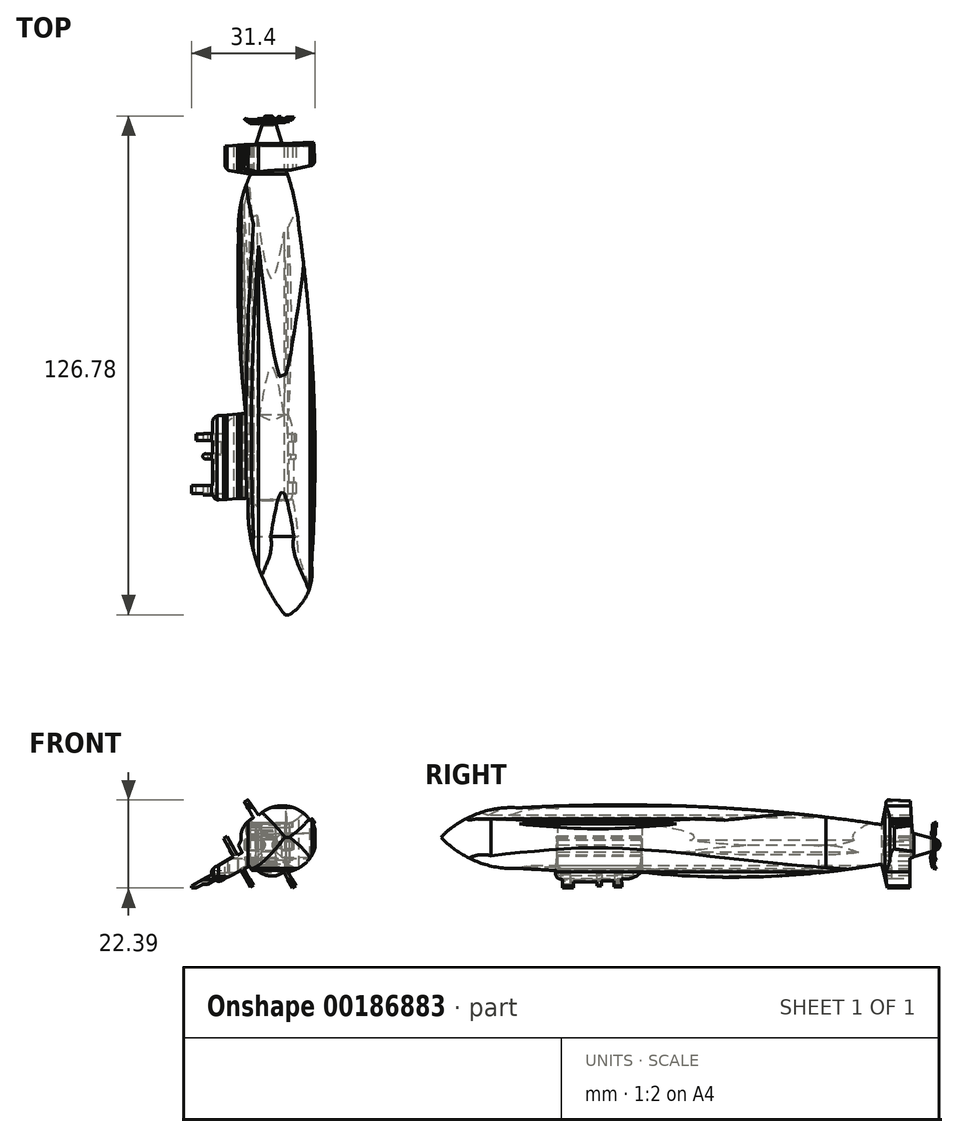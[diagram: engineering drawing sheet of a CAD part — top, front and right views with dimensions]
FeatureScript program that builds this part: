
annotation { "Feature Type Name" : "Feature", "Feature Type Description" : "" }
export const myFeature = defineFeature(function(context is Context, id is Id, definition is map)
    precondition{}
    {
        {
            var Q0;
            Q0=qCreatedBy(makeId("Front.planeOp"),FACE);
            var sketch = newSketch(context, id + "F0", { "sketchPlane" : qUnion([Q0])});
            skLineSegment(sketch, "E0.bottom", {"start": v(0, 0) * mm, "end": v(32, 0) * mm});
            skLineSegment(sketch, "E0.top", {"start": v(0, 23) * mm, "end": v(32, 23) * mm});
            skLineSegment(sketch, "E0.left", {"start": v(0, 0) * mm, "end": v(0, 23) * mm});
            skLineSegment(sketch, "E0.right", {"start": v(32, 0) * mm, "end": v(32, 23) * mm});
            skSolve(sketch);
        }
        {
            var Q0;
            Q0=makeQuery(id+"F0.imprint","IMPRINT",FACE,{"disambiguationData":[TD([[makeQuery(id+"F0.imprint","IMPRINT",EDGE,{"derivedFrom":sQuery(id+"F0.wireOp",EDGE,"E0.bottom")}),1.0]])]});
            extrude(context, id + "F1", {"entities" : qUnion([Q0]), "depth" : 128 * mm});
        }
        {
            var Q0;
            Q0=makeQuery(id+"F1.opExtrude","CAP_FACE",FACE,{"disambiguationData":[OSD([sQuery(id+"F0.wireOp",EDGE,"E0.bottom"),sQuery(id+"F0.wireOp",EDGE,"E0.top"),sQuery(id+"F0.wireOp",EDGE,"E0.left"),sQuery(id+"F0.wireOp",EDGE,"E0.right")])],"isStart":false});
            var sketch = newSketch(context, id + "F2", { "sketchPlane" : qUnion([Q0])});
            skArc(sketch, "E1", {"start": v(30.16, 17.5) * mm, "mid": v(23.9, 21.12) * mm, "end": v(17.06, 18.74) * mm});
            skArc(sketch, "E2", {"start": v(24.47, 4.4) * mm, "mid": v(30.73, 8.86) * mm, "end": v(30.92, 16.54) * mm});
            skArc(sketch, "E3", {"start": v(15.8, 18.1) * mm, "mid": v(13.22, 15.75) * mm, "end": v(12.66, 12.3) * mm});
            skArc(sketch, "E4", {"start": v(16.72, 4.8) * mm, "mid": v(20, 3.32) * mm, "end": v(23.48, 4.27) * mm});
            skArc(sketch, "E5", {"start": v(6.51, 5.84) * mm, "mid": v(5.36, 5.04) * mm, "end": v(5.1, 3.67) * mm});
            skArc(sketch, "E6", {"start": v(5.95, 2.34) * mm, "mid": v(7.24, 1.97) * mm, "end": v(8.4, 2.62) * mm});
            skLineSegment(sketch, "E7", {"start": v(15.8, 18.1) * mm, "end": v(13.43, 22.11) * mm});
            skLineSegment(sketch, "E8", {"start": v(13.43, 22.11) * mm, "end": v(14.36, 22.66) * mm});
            skLineSegment(sketch, "E9", {"start": v(14.36, 22.66) * mm, "end": v(17.06, 18.74) * mm});
            skLineSegment(sketch, "E10", {"start": v(30.16, 17.5) * mm, "end": v(30.65, 17.88) * mm});
            skLineSegment(sketch, "E11", {"start": v(30.65, 17.88) * mm, "end": v(31.35, 16.97) * mm});
            skLineSegment(sketch, "E12", {"start": v(31.35, 16.97) * mm, "end": v(30.92, 16.54) * mm});
            skLineSegment(sketch, "E13", {"start": v(24.47, 4.4) * mm, "end": v(26.52, 0.83) * mm});
            skLineSegment(sketch, "E14", {"start": v(26.52, 0.83) * mm, "end": v(25.64, 0.32) * mm});
            skLineSegment(sketch, "E15", {"start": v(25.64, 0.32) * mm, "end": v(23.48, 4.27) * mm});
            skLineSegment(sketch, "E16", {"start": v(12.66, 12.3) * mm, "end": v(11.92, 11.1) * mm});
            skLineSegment(sketch, "E17", {"start": v(11.92, 11.1) * mm, "end": v(12.92, 9.27) * mm});
            skLineSegment(sketch, "E18", {"start": v(12.92, 9.27) * mm, "end": v(11.77, 8.61) * mm});
            skLineSegment(sketch, "E19", {"start": v(11.77, 8.61) * mm, "end": v(9.03, 13.36) * mm});
            skLineSegment(sketch, "E20", {"start": v(9.03, 13.36) * mm, "end": v(8.12, 12.84) * mm});
            skLineSegment(sketch, "E21", {"start": v(8.12, 12.84) * mm, "end": v(10.64, 8.24) * mm});
            skLineSegment(sketch, "E22", {"start": v(10.64, 8.24) * mm, "end": v(6.51, 5.84) * mm});
            skLineSegment(sketch, "E23", {"start": v(5.1, 3.67) * mm, "end": v(0, 0.87) * mm});
            skLineSegment(sketch, "E24", {"start": v(0, 0.87) * mm, "end": v(0.73, 0) * mm});
            skLineSegment(sketch, "E25", {"start": v(0.73, 0) * mm, "end": v(2.91, 1.2) * mm});
            skLineSegment(sketch, "E26", {"start": v(2.91, 1.2) * mm, "end": v(4.06, 1.2) * mm});
            skLineSegment(sketch, "E27", {"start": v(4.06, 1.2) * mm, "end": v(5.95, 2.34) * mm});
            skLineSegment(sketch, "E28", {"start": v(8.4, 2.62) * mm, "end": v(12.66, 4.73) * mm});
            skLineSegment(sketch, "E29", {"start": v(12.66, 4.73) * mm, "end": v(15.01, 0.43) * mm});
            skLineSegment(sketch, "E30", {"start": v(15.01, 0.43) * mm, "end": v(15.8, 0.89) * mm});
            skLineSegment(sketch, "E31", {"start": v(15.8, 0.89) * mm, "end": v(13.39, 5.08) * mm});
            skLineSegment(sketch, "E32", {"start": v(13.39, 5.08) * mm, "end": v(14.7, 5.84) * mm});
            skLineSegment(sketch, "E33", {"start": v(14.7, 5.84) * mm, "end": v(15.34, 4.73) * mm});
            skLineSegment(sketch, "E34", {"start": v(15.34, 4.73) * mm, "end": v(16.72, 4.8) * mm});
            skLineSegment(sketch, "E35.bottom", {"start": v(32, 0) * mm, "end": v(0, 0) * mm});
            skLineSegment(sketch, "E35.top", {"start": v(32, 23) * mm, "end": v(0, 23) * mm});
            skLineSegment(sketch, "E35.left", {"start": v(32, 0) * mm, "end": v(32, 23) * mm});
            skLineSegment(sketch, "E35.right", {"start": v(0, 0) * mm, "end": v(0, 23) * mm});
            skSolve(sketch);
        }
        {
            var Q0;
            Q0=makeQuery(id+"F1.opExtrude","SWEPT_FACE",FACE,{"disambiguationData":[OSD([sQuery(id+"F0.wireOp",EDGE,"E0.right")])]});
            var sketch = newSketch(context, id + "F3", { "sketchPlane" : qUnion([Q0])});
            skArc(sketch, "E36", {"start": v(-107, 20.64) * mm, "mid": v(-117.76, 19.1) * mm, "end": v(-126.88, 13.18) * mm});
            skArc(sketch, "E37", {"start": v(-126.88, 13.18) * mm, "mid": v(-117.83, 7) * mm, "end": v(-107, 5.25) * mm});
            skArc(sketch, "E38", {"start": v(-14.85, 16.34) * mm, "mid": v(-60.81, 20.9) * mm, "end": v(-107, 20.64) * mm});
            skArc(sketch, "E39", {"start": v(-76.03, 4.3) * mm, "mid": v(-45.41, 3.13) * mm, "end": v(-14.95, 6.4) * mm});
            skArc(sketch, "E40", {"start": v(-97.6, 4.69) * mm, "mid": v(-102.3, 4.98) * mm, "end": v(-107, 5.25) * mm});
            skArc(sketch, "E41", {"start": v(-80.98, 2.6) * mm, "mid": v(-78.3, 2.84) * mm, "end": v(-76.03, 4.3) * mm});
            skArc(sketch, "E42", {"start": v(-97.6, 4.69) * mm, "mid": v(-97.48, 3.09) * mm, "end": v(-95.98, 2.52) * mm});
            skArc(sketch, "E43", {"start": v(-12.67, 22.6) * mm, "mid": v(-13.6, 22.45) * mm, "end": v(-13.82, 21.53) * mm});
            skArc(sketch, "E44", {"start": v(-1.45, 9.87) * mm, "mid": v(-0.1, 11.16) * mm, "end": v(-1.28, 12.6) * mm});
            skLineSegment(sketch, "E45", {"start": v(-95.98, 2.52) * mm, "end": v(-95.98, 0.27) * mm});
            skLineSegment(sketch, "E46", {"start": v(-95.98, 0.27) * mm, "end": v(-93.2, 0.27) * mm});
            skLineSegment(sketch, "E47", {"start": v(-93.2, 0.27) * mm, "end": v(-93.2, 1.83) * mm});
            skLineSegment(sketch, "E48", {"start": v(-93.2, 1.83) * mm, "end": v(-87.22, 1.83) * mm});
            skLineSegment(sketch, "E49", {"start": v(-87.22, 1.83) * mm, "end": v(-87.22, 0.87) * mm});
            skLineSegment(sketch, "E50", {"start": v(-87.22, 0.87) * mm, "end": v(-86.1, 0.87) * mm});
            skLineSegment(sketch, "E51", {"start": v(-86.1, 0.87) * mm, "end": v(-86.1, 2.04) * mm});
            skLineSegment(sketch, "E52", {"start": v(-86.1, 2.04) * mm, "end": v(-82.87, 2.04) * mm});
            skLineSegment(sketch, "E53", {"start": v(-82.87, 2.04) * mm, "end": v(-82.87, 0.54) * mm});
            skLineSegment(sketch, "E54", {"start": v(-82.87, 0.54) * mm, "end": v(-80.96, 0.54) * mm});
            skLineSegment(sketch, "E55", {"start": v(-80.96, 0.54) * mm, "end": v(-80.98, 2.6) * mm});
            skLineSegment(sketch, "E56", {"start": v(-13.82, 21.53) * mm, "end": v(-14.85, 16.34) * mm});
            skLineSegment(sketch, "E57", {"start": v(-12.67, 22.6) * mm, "end": v(-7.65, 22.39) * mm});
            skLineSegment(sketch, "E58", {"start": v(-7.65, 22.39) * mm, "end": v(-7.16, 14.2) * mm});
            skLineSegment(sketch, "E59", {"start": v(-7.16, 14.2) * mm, "end": v(-2.04, 12.84) * mm});
            skLineSegment(sketch, "E60", {"start": v(-2.04, 12.84) * mm, "end": v(-2.04, 13.5) * mm});
            skLineSegment(sketch, "E61", {"start": v(-2.04, 13.5) * mm, "end": v(-2.24, 13.63) * mm});
            skLineSegment(sketch, "E62", {"start": v(-2.24, 13.63) * mm, "end": v(-2.24, 14.68) * mm});
            skLineSegment(sketch, "E63", {"start": v(-2.24, 14.68) * mm, "end": v(-2.05, 14.98) * mm});
            skLineSegment(sketch, "E64", {"start": v(-2.05, 14.98) * mm, "end": v(-2.05, 16.5) * mm});
            skLineSegment(sketch, "E65", {"start": v(-2.05, 16.5) * mm, "end": v(-1.7, 16.77) * mm});
            skLineSegment(sketch, "E66", {"start": v(-1.7, 16.77) * mm, "end": v(-0.96, 16.98) * mm});
            skLineSegment(sketch, "E67", {"start": v(-0.96, 16.98) * mm, "end": v(-0.96, 15.6) * mm});
            skLineSegment(sketch, "E68", {"start": v(-0.96, 15.6) * mm, "end": v(-1.24, 15.6) * mm});
            skLineSegment(sketch, "E69", {"start": v(-1.24, 15.6) * mm, "end": v(-1.24, 13.99) * mm});
            skLineSegment(sketch, "E70", {"start": v(-1.24, 13.99) * mm, "end": v(-1.53, 13.41) * mm});
            skLineSegment(sketch, "E71", {"start": v(-1.53, 13.41) * mm, "end": v(-1.53, 12.84) * mm});
            skLineSegment(sketch, "E72", {"start": v(-1.53, 12.84) * mm, "end": v(-1.28, 12.6) * mm});
            skLineSegment(sketch, "E73", {"start": v(-1.45, 9.87) * mm, "end": v(-1.45, 8.08) * mm});
            skLineSegment(sketch, "E74", {"start": v(-1.45, 8.08) * mm, "end": v(-1.28, 8.04) * mm});
            skLineSegment(sketch, "E75", {"start": v(-1.28, 8.04) * mm, "end": v(-0.97, 7.47) * mm});
            skLineSegment(sketch, "E76", {"start": v(-0.97, 7.47) * mm, "end": v(-1.45, 7.2) * mm});
            skLineSegment(sketch, "E77", {"start": v(-1.45, 7.2) * mm, "end": v(-1.28, 6.87) * mm});
            skLineSegment(sketch, "E78", {"start": v(-1.28, 6.87) * mm, "end": v(-1.53, 6.74) * mm});
            skLineSegment(sketch, "E79", {"start": v(-1.53, 6.74) * mm, "end": v(-1.61, 6.12) * mm});
            skLineSegment(sketch, "E80", {"start": v(-1.61, 6.12) * mm, "end": v(-1.28, 5.79) * mm});
            skLineSegment(sketch, "E81", {"start": v(-1.28, 5.79) * mm, "end": v(-1.07, 5.09) * mm});
            skLineSegment(sketch, "E82", {"start": v(-1.07, 5.09) * mm, "end": v(-1.53, 5.2) * mm});
            skLineSegment(sketch, "E83", {"start": v(-1.53, 5.2) * mm, "end": v(-1.92, 5.31) * mm});
            skLineSegment(sketch, "E84", {"start": v(-1.92, 5.31) * mm, "end": v(-2.12, 5.72) * mm});
            skLineSegment(sketch, "E85", {"start": v(-2.12, 5.72) * mm, "end": v(-2.14, 6.03) * mm});
            skLineSegment(sketch, "E86", {"start": v(-2.14, 6.03) * mm, "end": v(-2.33, 6.22) * mm});
            skLineSegment(sketch, "E87", {"start": v(-2.33, 6.22) * mm, "end": v(-2.45, 7.34) * mm});
            skLineSegment(sketch, "E88", {"start": v(-2.45, 7.34) * mm, "end": v(-2.52, 8.06) * mm});
            skLineSegment(sketch, "E89", {"start": v(-2.52, 8.06) * mm, "end": v(-2.11, 9.6) * mm});
            skLineSegment(sketch, "E90", {"start": v(-2.11, 9.6) * mm, "end": v(-7.7, 7.84) * mm});
            skLineSegment(sketch, "E91", {"start": v(-7.7, 7.84) * mm, "end": v(-7.7, 0.27) * mm});
            skLineSegment(sketch, "E92", {"start": v(-7.7, 0.27) * mm, "end": v(-13.5, 0.27) * mm});
            skLineSegment(sketch, "E93", {"start": v(-13.5, 0.27) * mm, "end": v(-14.95, 6.4) * mm});
            skLineSegment(sketch, "E94.bottom", {"start": v(0, 0) * mm, "end": v(-128, 0) * mm});
            skLineSegment(sketch, "E94.top", {"start": v(0, 23) * mm, "end": v(-128, 23) * mm});
            skLineSegment(sketch, "E94.left", {"start": v(0, 0) * mm, "end": v(0, 23) * mm});
            skLineSegment(sketch, "E94.right", {"start": v(-128, 0) * mm, "end": v(-128, 23) * mm});
            skSolve(sketch);
        }
        {
            var Q0;
            Q0=makeQuery(id+"F1.opExtrude","SWEPT_FACE",FACE,{"disambiguationData":[OSD([sQuery(id+"F0.wireOp",EDGE,"E0.top")])]});
            var sketch = newSketch(context, id + "F4", { "sketchPlane" : qUnion([Q0])});
            skArc(sketch, "E95", {"start": v(14.45, -97.2) * mm, "mid": v(16.46, -113.17) * mm, "end": v(24.1, -127.33) * mm});
            skArc(sketch, "E96", {"start": v(24.1, -127.33) * mm, "mid": v(29.36, -121.77) * mm, "end": v(30.52, -114.21) * mm});
            skArc(sketch, "E97", {"start": v(30.52, -114.21) * mm, "mid": v(31.11, -71.55) * mm, "end": v(27.4, -29.05) * mm});
            skArc(sketch, "E98", {"start": v(27.4, -29.05) * mm, "mid": v(26.22, -21.46) * mm, "end": v(24.1, -14.07) * mm});
            skArc(sketch, "E99", {"start": v(15.08, -14.85) * mm, "mid": v(12.5, -22.7) * mm, "end": v(11.96, -30.92) * mm});
            skArc(sketch, "E100", {"start": v(11.96, -30.92) * mm, "mid": v(12.06, -53.34) * mm, "end": v(13.83, -75.68) * mm});
            skArc(sketch, "E101", {"start": v(5.56, -96.4) * mm, "mid": v(5.9, -97.3) * mm, "end": v(6.83, -97.63) * mm});
            skArc(sketch, "E102", {"start": v(7, -76.26) * mm, "mid": v(5.8, -76.77) * mm, "end": v(5.42, -78) * mm});
            skArc(sketch, "E103", {"start": v(3.64, -85.92) * mm, "mid": v(2.9, -86.48) * mm, "end": v(3.38, -87.27) * mm});
            skArc(sketch, "E104", {"start": v(30.1, -12.79) * mm, "mid": v(30.9, -12.48) * mm, "end": v(31.3, -11.7) * mm});
            skArc(sketch, "E105", {"start": v(8.5, -12.25) * mm, "mid": v(8.78, -13.37) * mm, "end": v(9.71, -14.04) * mm});
            skArc(sketch, "E106", {"start": v(20.92, -0.76) * mm, "mid": v(19.6, 0.16) * mm, "end": v(18.3, -0.79) * mm});
            skLineSegment(sketch, "E107", {"start": v(20.92, -0.76) * mm, "end": v(21.7, -0.76) * mm});
            skLineSegment(sketch, "E108", {"start": v(21.7, -0.76) * mm, "end": v(22.02, -0.33) * mm});
            skLineSegment(sketch, "E109", {"start": v(22.02, -0.33) * mm, "end": v(22.76, -0.33) * mm});
            skLineSegment(sketch, "E110", {"start": v(22.76, -0.33) * mm, "end": v(22.76, -0.76) * mm});
            skLineSegment(sketch, "E111", {"start": v(22.76, -0.76) * mm, "end": v(23.78, -0.76) * mm});
            skLineSegment(sketch, "E112", {"start": v(23.78, -0.76) * mm, "end": v(24.13, -0.45) * mm});
            skLineSegment(sketch, "E113", {"start": v(24.13, -0.45) * mm, "end": v(26.03, -0.45) * mm});
            skLineSegment(sketch, "E114", {"start": v(26.03, -0.45) * mm, "end": v(25.5, -1.22) * mm});
            skLineSegment(sketch, "E115", {"start": v(25.5, -1.22) * mm, "end": v(24.92, -1.22) * mm});
            skLineSegment(sketch, "E116", {"start": v(24.92, -1.22) * mm, "end": v(24.92, -1.54) * mm});
            skLineSegment(sketch, "E117", {"start": v(24.92, -1.54) * mm, "end": v(24.16, -1.54) * mm});
            skLineSegment(sketch, "E118", {"start": v(24.16, -1.54) * mm, "end": v(23.78, -1.84) * mm});
            skLineSegment(sketch, "E119", {"start": v(23.78, -1.84) * mm, "end": v(21.33, -1.84) * mm});
            skLineSegment(sketch, "E120", {"start": v(21.33, -1.84) * mm, "end": v(23.02, -7.13) * mm});
            skLineSegment(sketch, "E121", {"start": v(23.02, -7.13) * mm, "end": v(31.06, -6.76) * mm});
            skLineSegment(sketch, "E122", {"start": v(31.06, -6.76) * mm, "end": v(31.3, -11.7) * mm});
            skLineSegment(sketch, "E123", {"start": v(30.1, -12.79) * mm, "end": v(24.1, -14.07) * mm});
            skLineSegment(sketch, "E124", {"start": v(18.3, -0.79) * mm, "end": v(16.83, -0.79) * mm});
            skLineSegment(sketch, "E125", {"start": v(16.83, -0.79) * mm, "end": v(16.83, -1.03) * mm});
            skLineSegment(sketch, "E126", {"start": v(16.83, -1.03) * mm, "end": v(14.51, -1.03) * mm});
            skLineSegment(sketch, "E127", {"start": v(14.51, -1.03) * mm, "end": v(13.76, -0.79) * mm});
            skLineSegment(sketch, "E128", {"start": v(13.76, -0.79) * mm, "end": v(13.49, -0.98) * mm});
            skLineSegment(sketch, "E129", {"start": v(13.49, -0.98) * mm, "end": v(15, -2.1) * mm});
            skLineSegment(sketch, "E130", {"start": v(15, -2.1) * mm, "end": v(16.34, -2.1) * mm});
            skLineSegment(sketch, "E131", {"start": v(16.34, -2.1) * mm, "end": v(17, -2.2) * mm});
            skLineSegment(sketch, "E132", {"start": v(17, -2.2) * mm, "end": v(17.69, -1.7) * mm});
            skLineSegment(sketch, "E133", {"start": v(17.69, -1.7) * mm, "end": v(17.9, -2.47) * mm});
            skLineSegment(sketch, "E134", {"start": v(17.9, -2.47) * mm, "end": v(16.41, -7.27) * mm});
            skLineSegment(sketch, "E135", {"start": v(16.41, -7.27) * mm, "end": v(8.5, -7.75) * mm});
            skLineSegment(sketch, "E136", {"start": v(8.5, -7.75) * mm, "end": v(8.5, -12.25) * mm});
            skLineSegment(sketch, "E137", {"start": v(9.71, -14.04) * mm, "end": v(15.08, -14.85) * mm});
            skLineSegment(sketch, "E138", {"start": v(7, -76.26) * mm, "end": v(13.83, -75.68) * mm});
            skLineSegment(sketch, "E139", {"start": v(5.42, -78) * mm, "end": v(5.42, -80.78) * mm});
            skLineSegment(sketch, "E140", {"start": v(5.42, -80.78) * mm, "end": v(1.13, -80.78) * mm});
            skLineSegment(sketch, "E141", {"start": v(1.13, -80.78) * mm, "end": v(1.13, -82.64) * mm});
            skLineSegment(sketch, "E142", {"start": v(1.13, -82.64) * mm, "end": v(5.42, -82.64) * mm});
            skLineSegment(sketch, "E143", {"start": v(5.42, -82.64) * mm, "end": v(5.42, -85.97) * mm});
            skLineSegment(sketch, "E144", {"start": v(5.42, -85.97) * mm, "end": v(3.64, -85.92) * mm});
            skLineSegment(sketch, "E145", {"start": v(3.38, -87.27) * mm, "end": v(5.42, -87.27) * mm});
            skLineSegment(sketch, "E146", {"start": v(5.42, -87.27) * mm, "end": v(5.42, -94.04) * mm});
            skLineSegment(sketch, "E147", {"start": v(5.42, -94.04) * mm, "end": v(0, -94.04) * mm});
            skLineSegment(sketch, "E148", {"start": v(0, -94.04) * mm, "end": v(0, -94.83) * mm});
            skLineSegment(sketch, "E149", {"start": v(0, -94.83) * mm, "end": v(5.42, -94.54) * mm});
            skLineSegment(sketch, "E150", {"start": v(5.42, -94.54) * mm, "end": v(5.47, -95.43) * mm});
            skLineSegment(sketch, "E151", {"start": v(5.47, -95.43) * mm, "end": v(0, -95.43) * mm});
            skLineSegment(sketch, "E152", {"start": v(0, -95.43) * mm, "end": v(0, -96.31) * mm});
            skLineSegment(sketch, "E153", {"start": v(0, -96.31) * mm, "end": v(5.56, -96.4) * mm});
            skLineSegment(sketch, "E154.bottom", {"start": v(32, 0) * mm, "end": v(0, 0) * mm});
            skLineSegment(sketch, "E154.top", {"start": v(32, -128) * mm, "end": v(0, -128) * mm});
            skLineSegment(sketch, "E154.left", {"start": v(32, 0) * mm, "end": v(32, -128) * mm});
            skLineSegment(sketch, "E154.right", {"start": v(0, 0) * mm, "end": v(0, -128) * mm});
            skLineSegment(sketch, "E155", {"start": v(6.83, -97.63) * mm, "end": v(14.45, -97.2) * mm});
            skSolve(sketch);
        }
        {
            var Q0;
            Q0=makeQuery(id+"F2.imprint","IMPRINT",FACE,{"disambiguationData":[TD([[makeQuery(id+"F2.imprint","IMPRINT",EDGE,{"derivedFrom":sQuery(id+"F2.wireOp",EDGE,"E1")}),-1.0]])]});
            extrude(context, id + "F5", {"entities" : qUnion([Q0]), "operationType" : NewBodyOperationType.REMOVE, "endBound" : BoundingType.THROUGH_ALL, "oppositeDirection" : true, "depth" : 25.4 * mm});
        }
        {
            var Q0;
            Q0 = qSketchRegion(id + "F3", true);
            extrude(context, id + "F6", {"entities" : qUnion([Q0]), "operationType" : NewBodyOperationType.REMOVE, "endBound" : BoundingType.THROUGH_ALL, "oppositeDirection" : true, "depth" : 25.4 * mm});
        }
        {
            var Q0;
            Q0=makeQuery(id+"F4.imprint","IMPRINT",FACE,{"disambiguationData":[TD([[makeQuery(id+"F4.imprint","IMPRINT",EDGE,{"derivedFrom":sQuery(id+"F4.wireOp",EDGE,"E99")}),-1.0]])]});
            var Q1;
            Q1=makeQuery(id+"F4.imprint","IMPRINT",FACE,{"disambiguationData":[TD([[makeQuery(id+"F4.imprint","IMPRINT",EDGE,{"derivedFrom":sQuery(id+"F4.wireOp",EDGE,"E95")}),-1.0]])]});
            extrude(context, id + "F7", {"entities" : qUnion([Q0, Q1]), "operationType" : NewBodyOperationType.REMOVE, "endBound" : BoundingType.THROUGH_ALL, "oppositeDirection" : true, "depth" : 25.4 * mm});
        }
    });
